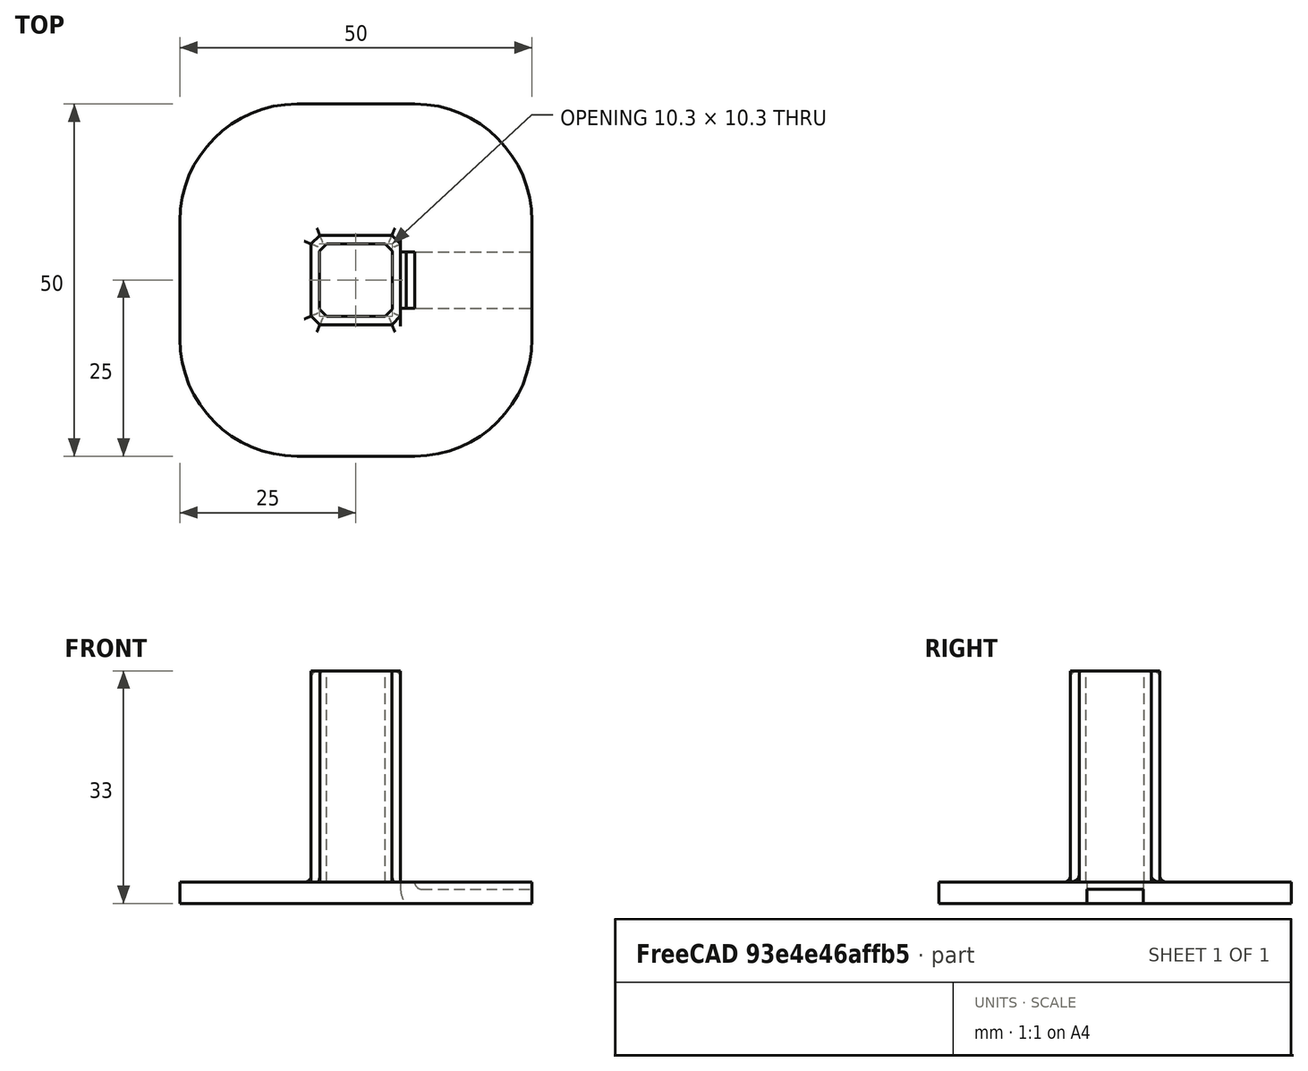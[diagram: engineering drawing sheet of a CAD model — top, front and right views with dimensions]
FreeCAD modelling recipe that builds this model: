
FCSTD DOCUMENT  (FreeCAD 0.18R13728 (Git))
Label: test110_3dlightstand
License: All rights reserved
LicenseURL: http://en.wikipedia.org/wiki/All_rights_reserved
objects: Sketcher::SketchObject×4, Part::Extrusion×4, Part::Cut×3, Part::Chamfer×1, Part::MultiFuse×1, Part::Fillet×1, Mesh::Feature×1
note: 14 computed .brp shape members not serialized (recipe doc carries the construction recipe); baked Part::Feature solids carry a one-line shape summary decoded from their .brp

FEATURE [Sketcher::SketchObject] Sketch001
  MapMode = 5
  Placement = pos=(0,0,0) rot=(1,0,0;3.14159rad)
  sketch-geometry (12):
    g0: LineSegment StartX=0 StartY=25 StartZ=0 EndX=8.36027 EndY=25 EndZ=0
    g1: LineSegment StartX=25 StartY=8.36027 StartZ=0 EndX=25 EndY=0 EndZ=0
    g2: ArcOfCircle CenterX=8.36027 CenterY=8.36027 CenterZ=0 NormalX=0 NormalY=0 NormalZ=1 AngleXU=0 Radius=16.6397 StartAngle=0 EndAngle=1.5708
    g3: LineSegment StartX=0 StartY=-25 StartZ=0 EndX=-8.36027 EndY=-25 EndZ=0
    g4: LineSegment StartX=-25 StartY=-8.36027 StartZ=0 EndX=-25 EndY=0 EndZ=0
    g5: ArcOfCircle CenterX=-8.36027 CenterY=-8.36027 CenterZ=0 NormalX=0 NormalY=0 NormalZ=1 AngleXU=0 Radius=16.6397 StartAngle=3.14159 EndAngle=4.71239
    g6: LineSegment StartX=0 StartY=25 StartZ=0 EndX=-8.36027 EndY=25 EndZ=0
    g7: LineSegment StartX=-25 StartY=8.36027 StartZ=0 EndX=-25 EndY=0 EndZ=0
    g8: ArcOfCircle CenterX=-8.36027 CenterY=8.36027 CenterZ=0 NormalX=0 NormalY=0 NormalZ=1 AngleXU=0 Radius=16.6397 StartAngle=1.5708 EndAngle=3.14159
    g9: LineSegment StartX=25 StartY=-8.36027 StartZ=0 EndX=25 EndY=0 EndZ=0
    g10: ArcOfCircle CenterX=8.36027 CenterY=-8.36027 CenterZ=0 NormalX=0 NormalY=0 NormalZ=1 AngleXU=0 Radius=16.6397 StartAngle=4.71239 EndAngle=6.28319
    g11: LineSegment StartX=0 StartY=-25 StartZ=0 EndX=8.36027 EndY=-25 EndZ=0
  constraints (31):
    c: PointOnObject(g0,g-2)
    c: PointOnObject(g1,g-1)
    c: Vertical(g1)
    c: Horizontal(g0)
    c: Tangent(g0,g2) = 1.5708
    c: Tangent(g1,g2) = 1.5708
    c: Equal(g0,g1)
    c: DistanceX(g-1,g1) = 25
    c: Vertical(g4)
    c: Horizontal(g3)
    c: Tangent(g3,g5) = 1.5708
    c: Tangent(g4,g5) = 1.5708
    c: Equal(g3,g4)
    c: Vertical(g7)
    c: Horizontal(g6)
    c: Tangent(g6,g8) = -1.5708
    c: Tangent(g7,g8) = -1.5708
    c: Equal(g6,g7)
    c: Vertical(g9)
    c: Horizontal(g11)
    c: Tangent(g11,g10) = -1.5708
    c: Tangent(g9,g10) = -1.5708
    c: Equal(g11,g9)
    c: Coincident(g6,g0)
    c: Coincident(g7,g4)
    c: Coincident(g3,g11)
    c: Coincident(g1,g9)
    c: Equal(g10,g2)
    c: Equal(g2,g8)
    c: Equal(g2,g5)
    c: Symmetric(g5,g2,g-1)
FEATURE [Sketcher::SketchObject] Sketch003
  MapMode = 5
  sketch-geometry (4):
    g0: LineSegment StartX=-5.15 StartY=-5.15 StartZ=0 EndX=5.15 EndY=-5.15 EndZ=0
    g1: LineSegment StartX=5.15 StartY=-5.15 StartZ=0 EndX=5.15 EndY=5.15 EndZ=0
    g2: LineSegment StartX=5.15 StartY=5.15 StartZ=0 EndX=-5.15 EndY=5.15 EndZ=0
    g3: LineSegment StartX=-5.15 StartY=5.15 StartZ=0 EndX=-5.15 EndY=-5.15 EndZ=0
  constraints (11):
    c: Coincident(g0,g1)
    c: Coincident(g1,g2)
    c: Coincident(g2,g3)
    c: Coincident(g3,g0)
    c: Horizontal(g0)
    c: Horizontal(g2)
    c: Vertical(g1)
    c: Vertical(g3)
    c: Symmetric(g3,g1,g-1)
    c: Equal(g1,g0)
    c: Distance(g1) = 10.3
FEATURE [Part::Extrusion] Extrude
  Base = -> Sketch003
  Dir = (0,0,1)
  DirMode = 2
  FaceMakerClass = Part::FaceMakerBullseye
  LengthFwd = 100
  LengthRev = 0
  Solid = true
  Symmetric = false
FEATURE [Part::Chamfer] Chamfer
  Base = -> Extrude
  Edges = 4 edges r=1: [Edge1,Edge2,Edge5,Edge8]
FEATURE [Part::Extrusion] Extrude002
  Base = -> Sketch001
  Dir = (0,0,-1)
  DirMode = 2
  FaceMakerClass = Part::FaceMakerBullseye
  LengthFwd = 3
  LengthRev = 0
  Solid = true
  Symmetric = false
FEATURE [Sketcher::SketchObject] Sketch002
  ExternalGeometry = -> [Chamfer]
  MapMode = 5
  Support = -> [Extrude002]
  sketch-geometry (14):
    g0: LineSegment StartX=-6.35 StartY=0 StartZ=0 EndX=-6.35 EndY=-5.11699 EndZ=0
    g1: LineSegment StartX=-5.11699 StartY=-6.35 StartZ=0 EndX=0 EndY=-6.35 EndZ=0
    g2: LineSegment StartX=-5.11699 StartY=-6.35 StartZ=0 EndX=-6.35 EndY=-5.11699 EndZ=0
    g3: LineSegment [constr] StartX=0 StartY=0 StartZ=0 EndX=-4.15 EndY=-5.15 EndZ=0
    g4: LineSegment StartX=6.35 StartY=0 StartZ=0 EndX=6.35 EndY=-5.11699 EndZ=0
    g5: LineSegment StartX=5.11699 StartY=-6.35 StartZ=0 EndX=6.35 EndY=-5.11699 EndZ=0
    g6: LineSegment StartX=5.11699 StartY=-6.35 StartZ=0 EndX=0 EndY=-6.35 EndZ=0
    g7: LineSegment StartX=5.11699 StartY=6.35 StartZ=0 EndX=0 EndY=6.35 EndZ=0
    g8: LineSegment StartX=5.11699 StartY=6.35 StartZ=0 EndX=6.35 EndY=5.11699 EndZ=0
    g9: LineSegment StartX=6.35 StartY=0 StartZ=0 EndX=6.35 EndY=5.11699 EndZ=0
    g10: LineSegment StartX=-5.11699 StartY=6.35 StartZ=0 EndX=0 EndY=6.35 EndZ=0
    g11: LineSegment StartX=-5.11699 StartY=6.35 StartZ=0 EndX=-6.35 EndY=5.11699 EndZ=0
    g12: LineSegment StartX=-6.35 StartY=0 StartZ=0 EndX=-6.35 EndY=5.11699 EndZ=0
    g13: GeomPoint X=-4.15 Y=-5.15 Z=0
  constraints (39):
    c: PointOnObject(g0,g-1)
    c: Vertical(g0)
    c: PointOnObject(g1,g-2)
    c: Horizontal(g1)
    c: Coincident(g2,g1)
    c: Coincident(g2,g0)
    c: Angle(g2,g-1) = 0.785398
    c: Equal(g0,g1)
    c: Coincident(g3,g-1)
    c: PointOnObject(g1,g3)
    c: Vertical(g4)
    c: Horizontal(g6)
    c: Coincident(g5,g6)
    c: Coincident(g5,g4)
    c: Equal(g4,g6)
    c: Vertical(g9)
    c: Horizontal(g7)
    c: Coincident(g8,g7)
    c: Coincident(g8,g9)
    c: Equal(g9,g7)
    c: Vertical(g12)
    c: Horizontal(g10)
    c: Coincident(g11,g10)
    c: Coincident(g11,g12)
    c: Equal(g12,g10)
    c: Parallel(g8,g2)
    c: Coincident(g10,g7)
    c: Coincident(g12,g0)
    c: Coincident(g9,g4)
    c: Coincident(g6,g1)
    c: Equal(g2,g5)
    c: Equal(g2,g8)
    c: Equal(g2,g11)
    c: Perpendicular(g2,g11)
    c: Perpendicular(g2,g5)
    c: PointOnObject(g7,g-2)
    c: Coincident(g13,g-3)
    c: Coincident(g3,g13)
    c: DistanceX(g0,g-4) = 1.2
FEATURE [Part::Extrusion] Extrude003
  Base = -> Sketch002
  Dir = (0,0,1)
  DirMode = 2
  FaceMakerClass = Part::FaceMakerBullseye
  LengthFwd = 30
  LengthRev = 0
  Solid = true
  Symmetric = false
FEATURE [Part::MultiFuse] Fusion
  Shapes = -> [Extrude003,Extrude002]
FEATURE [Part::Cut] Cut
  Base = -> Fusion
  Tool = -> Chamfer
FEATURE [Sketcher::SketchObject] Sketch
  ExternalGeometry = -> [Cut]
  Placement = pos=(0,0,0) rot=(1,0,0;1.5708rad)
  sketch-geometry (7):
    g0: LineSegment StartX=6.35 StartY=0 StartZ=0 EndX=6.35 EndY=-1 EndZ=0
    g1: LineSegment StartX=7.11393 StartY=-3 StartZ=0 EndX=25 EndY=-3 EndZ=0
    g2: LineSegment StartX=9.35 StartY=-1 StartZ=0 EndX=25 EndY=-1 EndZ=0
    g3: ArcOfCircle CenterX=9.35 CenterY=0 CenterZ=0 NormalX=0 NormalY=0 NormalZ=1 AngleXU=0 Radius=1 StartAngle=3.14159 EndAngle=4.71239
    g4: ArcOfCircle CenterX=9.35 CenterY=-1 CenterZ=0 NormalX=0 NormalY=0 NormalZ=1 AngleXU=0 Radius=3 StartAngle=3.14159 EndAngle=3.87132
    g5: LineSegment StartX=6.35 StartY=0 StartZ=0 EndX=8.35 EndY=0 EndZ=0
    g6: LineSegment StartX=25 StartY=-3 StartZ=0 EndX=25 EndY=-1 EndZ=0
  constraints (18):
    c: Coincident(g0,g-4)
    c: Vertical(g0)
    c: Coincident(g1,g-3)
    c: Horizontal(g1)
    c: PointOnObject(g5,g-1)
    c: PointOnObject(g2,g-3)
    c: Horizontal(g2)
    c: Tangent(g2,g3) = -1.5708
    c: Tangent(g0,g4) = -1.5708
    c: Coincident(g5,g0)
    c: Coincident(g6,g1)
    c: Coincident(g6,g2)
    c: Equal(g5,g6)
    c: Distance(g5) = 2
    c: Coincident(g3,g5)
    c: PointOnObject(g3,g-1)
    c: Coincident(g1,g4)
    c: Coincident(g4,g2)
FEATURE [Part::Extrusion] Extrude004
  Base = -> Sketch
  Dir = (0,-1,0)
  DirMode = 2
  FaceMakerClass = Part::FaceMakerBullseye
  LengthFwd = 8
  LengthRev = 0
  Solid = true
  Symmetric = true
FEATURE [Part::Cut] Cut001
  Base = -> Cut
  Tool = -> Extrude004
FEATURE [Part::Cut] Cut002
  Base = -> Cut
  Tool = -> Extrude004
FEATURE [Part::Fillet] Fillet
  Base = -> Cut002
  Edges = 15 edges r=1: [Edge2,Edge3,Edge4,Edge7,Edge8,Edge9,Edge10,Edge12,Edge22,Edge27,Edge29,Edge30,Edge32,Edge38,Edge40]
FEATURE [Mesh::Feature] Mesh  label="Fillet (Meshed)"
